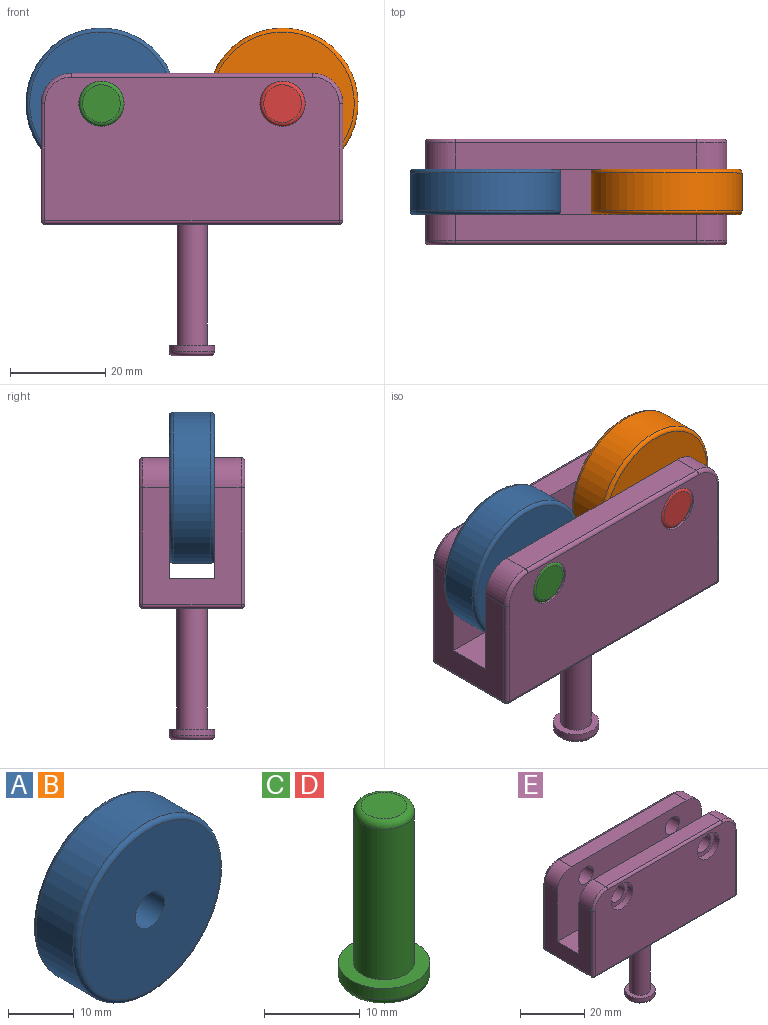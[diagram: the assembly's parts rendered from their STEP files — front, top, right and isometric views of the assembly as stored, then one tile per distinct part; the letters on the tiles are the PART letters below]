
ASSEMBLY  parts=5 mates=8
PART A: 6 faces, bbox 34.4x9.5x34.4 mm
  f0: cylinder r=3.17mm len=9.53mm, axis (0,1,0), area 190mm2, adj f2,f3
  f1: cylinder r=15.88mm len=31.75mm, axis (0,1,0), area 792mm2, adj f4,f5
  f2: plane 30.17x30.17mm, normal (0,-1,0), area 683mm2, adj f0,f5
  f3: plane 30.17x30.17mm, normal (0,1,0), area 683mm2, adj f0,f4
  f4: torus R=15.08mm, axis (0,-1,0), area 121.9mm2, adj f1,f3
  f5: torus R=15.08mm, axis (0,-1,0), area 121.9mm2, adj f1,f2
PART B: same geometry as A
PART C: 7 faces, bbox 10.3x10.3x22.2 mm
  f0: cylinder r=4.76mm len=9.53mm, axis (0,0,-1), area 42.8mm2, adj f1,f6
  f1: plane 9.53x9.53mm, normal (0,0,1), area 39.6mm2, adj f0,f3
  f2: plane 7.94x7.94mm, normal (0,0,-1), area 49.5mm2, adj f6
  f3: cylinder r=3.17mm len=19.21mm, axis (0,0,-1), area 383.2mm2, adj f1,f5
  f4: plane 4.76x4.76mm, normal (0,0,1), area 17.8mm2, adj f5
  f5: torus R=2.38mm, axis (0,0,1), area 22.6mm2, adj f3,f4
  f6: torus R=3.97mm, axis (0,0,1), area 35mm2, adj f0,f2
PART D: same geometry as C
PART E: 45 faces, bbox 64.5x22.2x59.9 mm
  f0: cylinder r=3.17mm len=6.35mm, axis (0,-1,0), area 82.3mm2, adj f10,f21
  f1: cylinder r=3.17mm len=6.35mm, axis (0,-1,0), area 82.3mm2, adj f10,f19
  f2: plane 63.5x9.53mm, normal (0,0,1), area 604.8mm2, adj f4,f6,f8,f10
  f3: plane 61.92x30.17mm, normal (0,1,0), area 1791.1mm2, adj f16,f17,f26,f27,f28,f30,f33,f34
  f4: plane 24.61x20.64mm, normal (-1,0,0), area 326.4mm2, adj f2,f8,f10,f22,f24,f34,f40,f43
  f5: plane 61.92x30.17mm, normal (0,-1,0), area 1711.9mm2, adj f18,f20,f31,f35,f38,f39,f41,f43
  f6: plane 24.61x20.64mm, normal (1,0,0), area 326.4mm2, adj f2,f8,f10,f23,f25,f27,f31,f32
  f7: plane 61.92x20.64mm, normal (0,0,-1), area 1246.3mm2, adj f12,f32,f33,f39,f40
  f8: plane 63.5x25.4mm, normal (0,-1,0), area 1532.3mm2, adj f2,f4,f6,f9,f16,f17,f22,f23
  f9: plane 50.8x5.56mm, normal (0,0,1), area 282.3mm2, adj f8,f22,f23,f28
  f10: plane 63.5x25.4mm, normal (0,1,0), area 1532.3mm2, adj f0,f1,f2,f4,f6,f11,f24,f25
  f11: plane 50.8x5.56mm, normal (0,0,1), area 282.3mm2, adj f10,f24,f25,f38
  f12: cylinder r=3.17mm len=25.4mm, axis (0,0,1), area 506.7mm2, adj f7,f15
  f13: cylinder r=4.76mm len=9.53mm, axis (0,0,1), area 42.8mm2, adj f15,f44
  f14: plane 7.94x7.94mm, normal (0,0,-1), area 49.5mm2, adj f44
  f15: plane 9.53x9.53mm, normal (0,0,1), area 39.6mm2, adj f12,f13
  f16: cylinder r=3.17mm len=6.35mm, axis (0,-1,0), area 126.7mm2, adj f3,f8
  f17: cylinder r=3.17mm len=6.35mm, axis (0,-1,0), area 126.7mm2, adj f3,f8
  f18: cylinder r=4.76mm len=9.53mm, axis (0,-1,0), area 66.5mm2, adj f5,f19
  f19: plane 9.53x9.53mm, normal (0,-1,0), area 39.6mm2, adj f1,f18
  f20: cylinder r=4.76mm len=9.53mm, axis (0,-1,0), area 66.5mm2, adj f5,f21
  f21: plane 9.53x9.53mm, normal (0,-1,0), area 39.6mm2, adj f0,f20
  f22: cylinder r=6.35mm len=6.35mm, axis (0,1,0), area 55.4mm2, adj f4,f8,f9,f30
  f23: cylinder r=6.35mm len=6.35mm, axis (0,-1,0), area 55.4mm2, adj f6,f8,f9,f26
  f24: cylinder r=6.35mm len=6.35mm, axis (0,1,0), area 55.4mm2, adj f4,f10,f11,f41
  f25: cylinder r=6.35mm len=6.35mm, axis (0,-1,0), area 55.4mm2, adj f6,f10,f11,f35
  f26: torus R=5.56mm, axis (0,1,0), area 11.9mm2, adj f3,f23,f27,f28
  f27: cylinder r=0.79mm len=24.61mm, axis (0,0,-1), area 30.6mm2, adj f3,f6,f26,f29
  f28: cylinder r=0.79mm len=50.8mm, axis (1,0,0), area 63.2mm2, adj f3,f9,f26,f30
  f29: sphere r=0.79mm, area 1mm2, adj f27,f32,f33
  f30: torus R=5.56mm, axis (0,1,0), area 11.9mm2, adj f3,f22,f28,f34
  f31: cylinder r=0.79mm len=24.61mm, axis (0,0,1), area 30.6mm2, adj f5,f6,f35,f36
  f32: cylinder r=0.79mm len=20.64mm, axis (0,1,0), area 25.7mm2, adj f6,f7,f29,f36
  f33: cylinder r=0.79mm len=61.92mm, axis (-1,0,0), area 77.1mm2, adj f3,f7,f29,f37
  f34: cylinder r=0.79mm len=24.61mm, axis (0,0,1), area 30.6mm2, adj f3,f4,f30,f37
  f35: torus R=5.56mm, axis (0,1,0), area 11.9mm2, adj f5,f25,f31,f38
  f36: sphere r=0.79mm, area 1mm2, adj f31,f32,f39
  f37: sphere r=0.79mm, area 1mm2, adj f33,f34,f40
  f38: cylinder r=0.79mm len=50.8mm, axis (-1,0,0), area 63.2mm2, adj f5,f11,f35,f41
  f39: cylinder r=0.79mm len=61.92mm, axis (1,0,0), area 77.1mm2, adj f5,f7,f36,f42
  f40: cylinder r=0.79mm len=20.64mm, axis (0,-1,0), area 25.7mm2, adj f4,f7,f37,f42
  f41: torus R=5.56mm, axis (0,1,0), area 11.9mm2, adj f5,f24,f38,f43
  f42: sphere r=0.79mm, area 1mm2, adj f39,f40,f43
  f43: cylinder r=0.79mm len=24.61mm, axis (0,0,-1), area 30.6mm2, adj f4,f5,f41,f42
  f44: torus R=3.97mm, axis (0,0,-1), area 35mm2, adj f13,f14
PLACE A t=(38.01,-12.44,12.85)mm
PLACE B t=(76.11,-12.44,12.85)mm
PLACE C rot(axis=(-1,0,0),90deg) t=(28.46,-28.31,58.35)mm
PLACE D rot(axis=(-1,0,0),90deg) t=(66.56,-28.31,58.35)mm
PLACE E t=(33.16,-17.86,13.07)mm
MATE planar A.f0 <-> E.f8  axis (0,1,0) through (7.14,-12.44,38.47)mm
MATE cylindrical A.f0 <-> C.f0  axis (0,-1,0) through (7.14,-21.96,38.47)mm
MATE cylindrical B.f0 <-> E.f0  axis (0,1,0) through (45.24,-12.44,38.47)mm
MATE planar D.f0 <-> E.f0  axis (0,1,0) through (45.24,-26.09,38.47)mm
MATE cylindrical D.f0 <-> E.f0  axis (0,1,0) through (45.24,-6.09,38.47)mm
MATE cylindrical C.f0 <-> E.f1  axis (0,1,0) through (7.14,-6.09,38.47)mm
MATE planar C.f0 <-> E.f1  axis (0,1,0) through (7.14,-26.09,38.47)mm
MATE planar B.f0 <-> E.f8  axis (0,1,0) through (45.24,-12.44,38.47)mm
